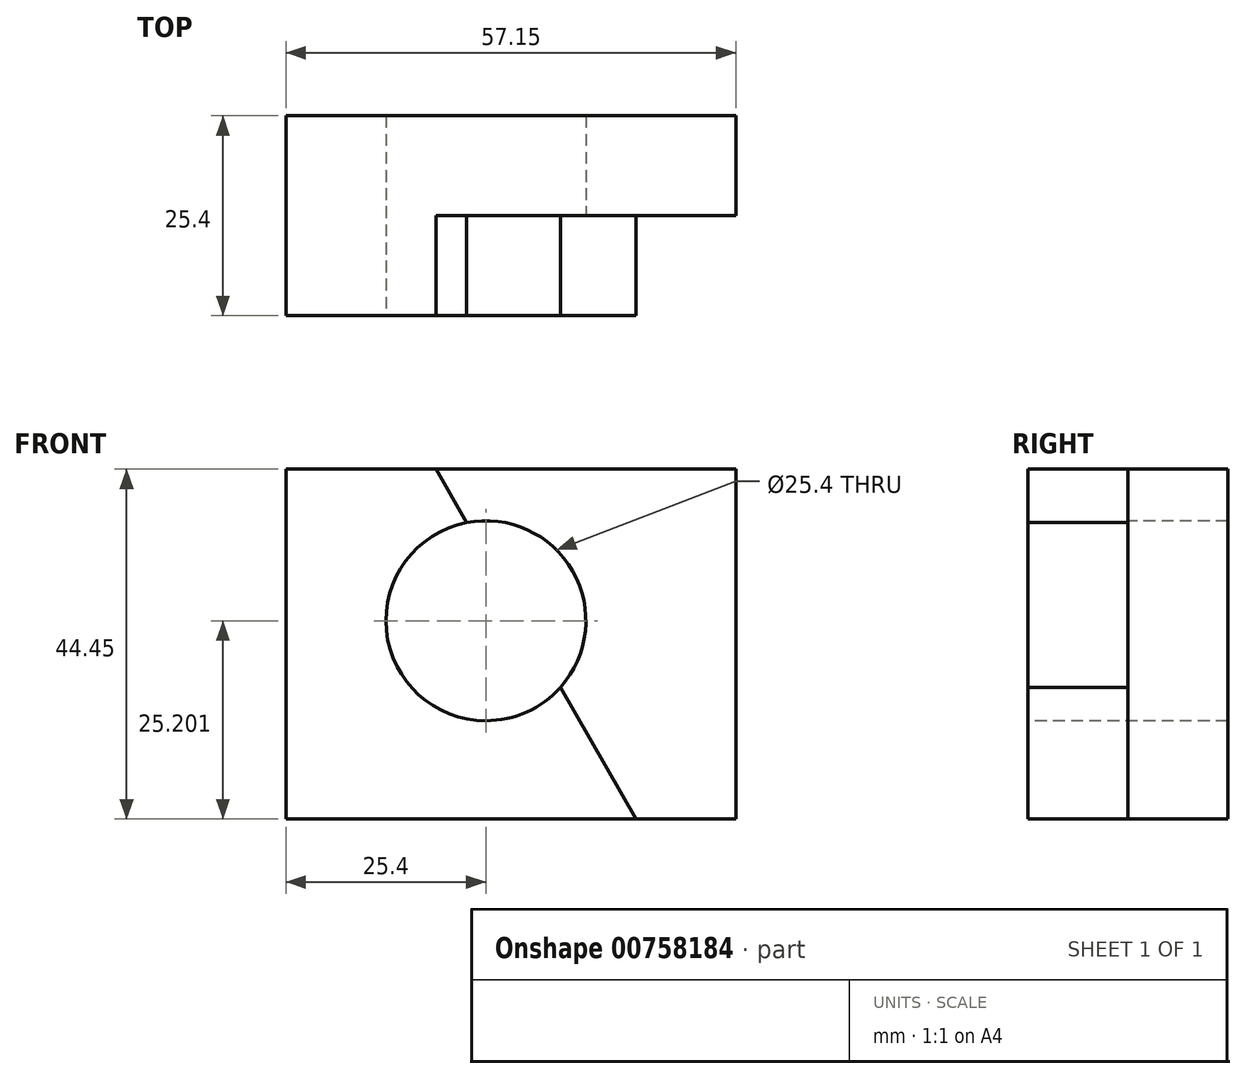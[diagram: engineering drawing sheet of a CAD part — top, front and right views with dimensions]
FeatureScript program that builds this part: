
annotation { "Feature Type Name" : "Feature", "Feature Type Description" : "" }
export const myFeature = defineFeature(function(context is Context, id is Id, definition is map)
    precondition{}
    {
        {
            var Q0;
            Q0=qCreatedBy(makeId("Front.planeOp"),FACE);
            var sketch = newSketch(context, id + "F0", { "sketchPlane" : qUnion([Q0])});
            skLineSegment(sketch, "E0", {"start": v(0, 0) * mm, "end": v(0, 44.45) * mm});
            skLineSegment(sketch, "E1", {"start": v(0, 44.45) * mm, "end": v(57.15, 44.45) * mm});
            skLineSegment(sketch, "E2", {"start": v(57.15, 44.45) * mm, "end": v(57.15, 0) * mm});
            skLineSegment(sketch, "E3", {"start": v(57.15, 0) * mm, "end": v(0, 0) * mm});
            skSolve(sketch);
        }
        {
            var Q0;
            Q0 = qSketchRegion(id + "F0", true);
            extrude(context, id + "F1", {"entities" : qUnion([Q0]), "oppositeDirection" : true, "depth" : 25.4 * mm, "offsetDistance" : 25.4 * mm});
        }
        {
            var Q0;
            Q0=makeQuery(id+"F1.opExtrude","CAP_FACE",FACE,{"disambiguationData":[OSD([sQuery(id+"F0.wireOp",EDGE,"E0"),sQuery(id+"F0.wireOp",EDGE,"E1"),sQuery(id+"F0.wireOp",EDGE,"E2"),sQuery(id+"F0.wireOp",EDGE,"E3")])],"isStart":true});
            var sketch = newSketch(context, id + "F2", { "sketchPlane" : qUnion([Q0])});
            skCircle(sketch, "E4", {"center": v(25.4, 25.2) * mm, "radius": 12.7 * mm});
            skLineSegment(sketch, "E5", {"start": v(19.05, 44.45) * mm, "end": v(44.45, 0) * mm});
            skSolve(sketch);
        }
        {
            var Q0;
            {var subQ0=sQuery(id+"F2.wireOp",EDGE,"E5");var subQ1=sQuery(id+"F2.wireOp",EDGE,"E4");var subQ2=makeQuery(id+"F2.imprint","INTERSECT",VERTEX,{"disambiguationData":[OD(0.0)],"derivedFrom":[subQ1,subQ0]});Q0=makeQuery(id+"F2.imprint","IMPRINT",FACE,{"disambiguationData":[TD([[makeQuery(id+"F2.imprint","IMPRINT",EDGE,{"disambiguationData":[TD([[subQ2,1.0]])],"derivedFrom":subQ1}),1.0]])]});}
            var Q1;
            {var subQ0=sQuery(id+"F2.wireOp",EDGE,"E5");var subQ1=sQuery(id+"F2.wireOp",EDGE,"E4");var subQ2=makeQuery(id+"F2.imprint","INTERSECT",VERTEX,{"disambiguationData":[OD(0.0)],"derivedFrom":[subQ1,subQ0]});Q1=makeQuery(id+"F2.imprint","IMPRINT",FACE,{"disambiguationData":[TD([[makeQuery(id+"F2.imprint","IMPRINT",EDGE,{"disambiguationData":[TD([[subQ2,-1.0]])],"derivedFrom":subQ1}),1.0]])]});}
            extrude(context, id + "F3", {"entities" : qUnion([Q0, Q1]), "operationType" : NewBodyOperationType.REMOVE, "oppositeDirection" : true, "depth" : 50.8 * mm, "offsetDistance" : 25.4 * mm});
        }
        {
            var Q0;
            Q0=makeQuery(id+"F1.opExtrude","CAP_FACE",FACE,{"disambiguationData":[OSD([sQuery(id+"F0.wireOp",EDGE,"E0"),sQuery(id+"F0.wireOp",EDGE,"E1"),sQuery(id+"F0.wireOp",EDGE,"E2"),sQuery(id+"F0.wireOp",EDGE,"E3")])],"isStart":true});
            var sketch = newSketch(context, id + "F4", { "sketchPlane" : qUnion([Q0])});
            skLineSegment(sketch, "E6", {"start": v(19.05, 44.45) * mm, "end": v(44.45, 0) * mm});
            skSolve(sketch);
        }
        {
            var Q0;
            Q0 = qSketchRegion(id + "F4", true);
            var Q1;
            {var subQ0=makeQuery(id+"F1.opExtrude","CAP_EDGE",EDGE,{"disambiguationData":[OSD([sQuery(id+"F0.wireOp",EDGE,"E2")])],"isStart":true});Q1=makeQuery(id+"F4.imprint","IMPRINT",FACE,{"disambiguationData":[TD([[makeQuery(id+"F4.imprint","IMPRINT",EDGE,{"derivedFrom":subQ0}),-1.0]])]});}
            extrude(context, id + "F5", {"entities" : qUnion([Q0, Q1]), "operationType" : NewBodyOperationType.REMOVE, "oppositeDirection" : true, "depth" : 12.7 * mm, "offsetDistance" : 25.4 * mm});
        }
    });
